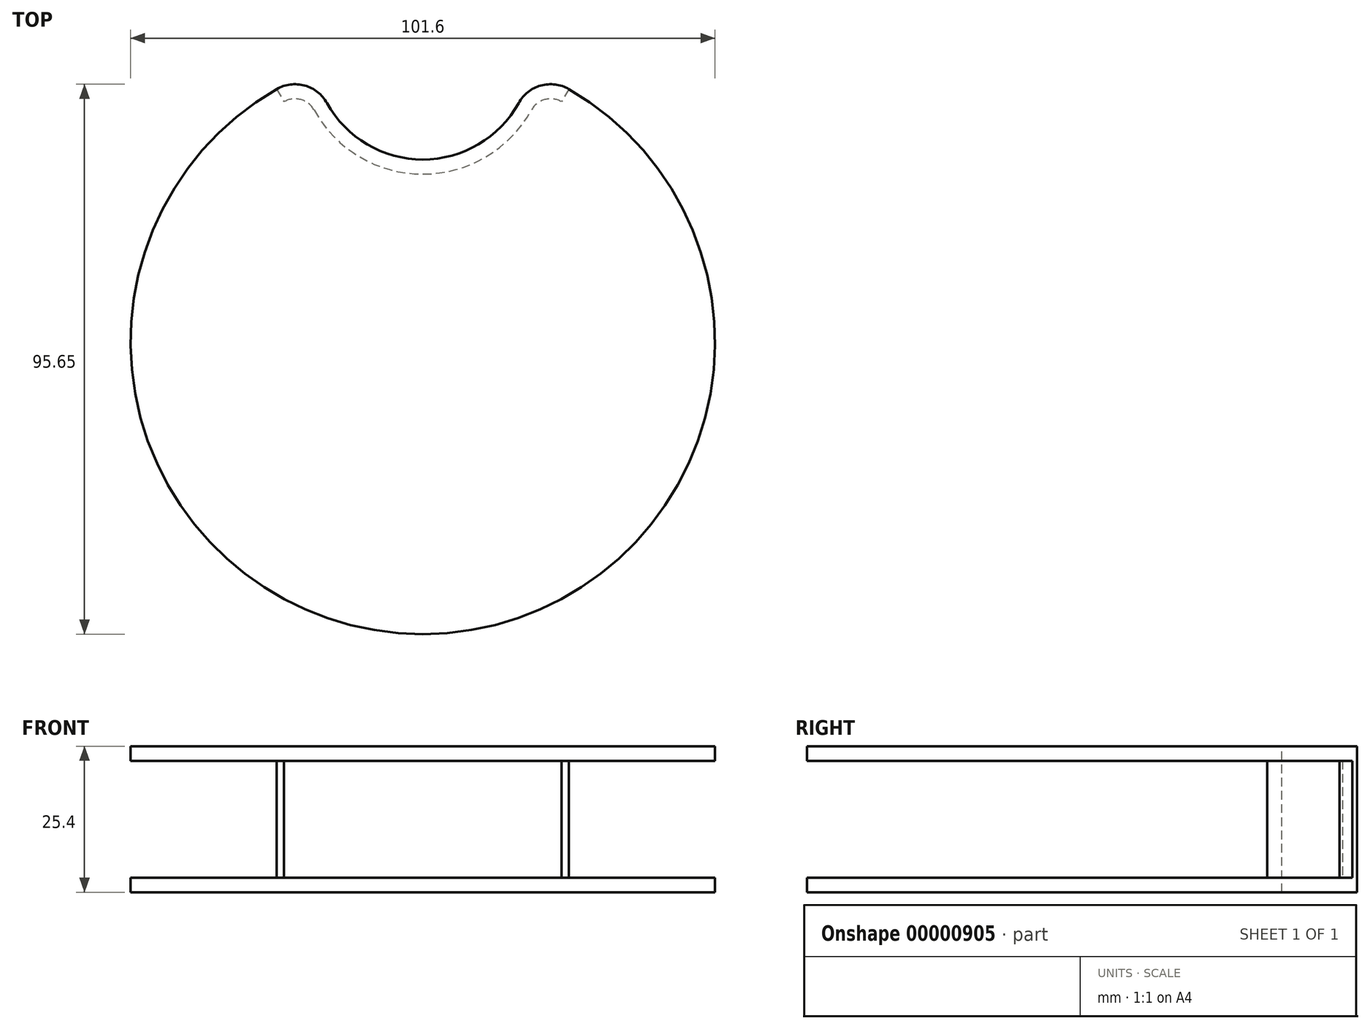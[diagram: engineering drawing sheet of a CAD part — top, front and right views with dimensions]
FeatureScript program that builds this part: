
annotation { "Feature Type Name" : "Feature", "Feature Type Description" : "" }
export const myFeature = defineFeature(function(context is Context, id is Id, definition is map)
    precondition{}
    {
        {
            var Q0;
            Q0=qCreatedBy(makeId("Top.planeOp"),FACE);
            var sketch = newSketch(context, id + "F0", { "sketchPlane" : qUnion([Q0])});
            skCircle(sketch, "E0", {"center": v(0, 0) * mm, "radius": 50.8 * mm});
            skSolve(sketch);
        }
        {
            var Q0;
            Q0 = qSketchRegion(id + "F0", true);
            extrude(context, id + "F1", {"entities" : qUnion([Q0]), "depth" : 25.4 * mm, "symmetric" : true});
        }
        {
            var Q0;
            Q0=makeQuery(id+"F1.opExtrude","CAP_FACE",FACE,{"disambiguationData":[OSD([sQuery(id+"F0.wireOp",EDGE,"E0")])],"isStart":false});
            var sketch = newSketch(context, id + "F2", { "sketchPlane" : qUnion([Q0])});
            skCircle(sketch, "E1", {"center": v(0, 50.8) * mm, "radius": 19.05 * mm});
            skSolve(sketch);
        }
        {
            var Q0;
            Q0 = qSketchRegion(id + "F2", true);
            extrude(context, id + "F3", {"entities" : qUnion([Q0]), "operationType" : NewBodyOperationType.REMOVE, "endBound" : BoundingType.THROUGH_ALL, "oppositeDirection" : true, "depth" : 25.4 * mm});
        }
        {
            var Q0;
            Q0=makeQuery(id+"F3.boolean.opBoolean","INTERSECT",EDGE,{"disambiguationData":[OD(0.0)],"derivedFrom":[makeQuery(id+"F1.opExtrude","SWEPT_FACE",FACE,{"disambiguationData":[OSD([sQuery(id+"F0.wireOp",EDGE,"E0")])]}),makeQuery(id+"F3.opExtrude","SWEPT_FACE",FACE,{"disambiguationData":[OSD([sQuery(id+"F2.wireOp",EDGE,"E1")])]})]});
            var Q1;
            Q1=makeQuery(id+"F3.boolean.opBoolean","INTERSECT",EDGE,{"disambiguationData":[OD(1.0)],"derivedFrom":[makeQuery(id+"F1.opExtrude","SWEPT_FACE",FACE,{"disambiguationData":[OSD([sQuery(id+"F0.wireOp",EDGE,"E0")])]}),makeQuery(id+"F3.opExtrude","SWEPT_FACE",FACE,{"disambiguationData":[OSD([sQuery(id+"F2.wireOp",EDGE,"E1")])]})]});
            var Q2;
            Q2=makeQuery(id+"FYpLOodkCXIoDKC_1.2.F3.boolean.opBoolean","INTERSECT",EDGE,{"disambiguationData":[OD(0.0)],"derivedFrom":[makeQuery(id+"FYpLOodkCXIoDKC_1.1.F3.boolean.opBoolean","SPLIT",FACE,{"disambiguationData":[OD(0.0)],"derivedFrom":makeQuery(id+"F1.opExtrude","SWEPT_FACE",FACE,{"disambiguationData":[OSD([sQuery(id+"F0.wireOp",EDGE,"E0")])]})}),makeQuery(id+"FYpLOodkCXIoDKC_1.2.F3.opExtrude","SWEPT_FACE",FACE,{"disambiguationData":[OSD([sQuery(id+"F2.wireOp",EDGE,"E1")])]})]});
            var Q3;
            Q3=makeQuery(id+"FYpLOodkCXIoDKC_1.2.F3.boolean.opBoolean","INTERSECT",EDGE,{"disambiguationData":[OD(1.0)],"derivedFrom":[makeQuery(id+"FYpLOodkCXIoDKC_1.1.F3.boolean.opBoolean","SPLIT",FACE,{"disambiguationData":[OD(0.0)],"derivedFrom":makeQuery(id+"F1.opExtrude","SWEPT_FACE",FACE,{"disambiguationData":[OSD([sQuery(id+"F0.wireOp",EDGE,"E0")])]})}),makeQuery(id+"FYpLOodkCXIoDKC_1.2.F3.opExtrude","SWEPT_FACE",FACE,{"disambiguationData":[OSD([sQuery(id+"F2.wireOp",EDGE,"E1")])]})]});
            var Q4;
            Q4=makeQuery(id+"FYpLOodkCXIoDKC_1.1.F3.boolean.opBoolean","INTERSECT",EDGE,{"disambiguationData":[OD(0.0)],"derivedFrom":[makeQuery(id+"F1.opExtrude","SWEPT_FACE",FACE,{"disambiguationData":[OSD([sQuery(id+"F0.wireOp",EDGE,"E0")])]}),makeQuery(id+"FYpLOodkCXIoDKC_1.1.F3.opExtrude","SWEPT_FACE",FACE,{"disambiguationData":[OSD([sQuery(id+"F2.wireOp",EDGE,"E1")])]})]});
            var Q5;
            Q5=makeQuery(id+"FYpLOodkCXIoDKC_1.1.F3.boolean.opBoolean","INTERSECT",EDGE,{"disambiguationData":[OD(1.0)],"derivedFrom":[makeQuery(id+"F1.opExtrude","SWEPT_FACE",FACE,{"disambiguationData":[OSD([sQuery(id+"F0.wireOp",EDGE,"E0")])]}),makeQuery(id+"FYpLOodkCXIoDKC_1.1.F3.opExtrude","SWEPT_FACE",FACE,{"disambiguationData":[OSD([sQuery(id+"F2.wireOp",EDGE,"E1")])]})]});
            fillet(context, id + "F4", {"entities" : qUnion([Q0, Q1, Q2, Q3, Q4, Q5]), "radius" : 6.35 * mm, "tangentPropagation" : true, "allowEdgeOverflow" : false});
        }
        {
            var Q0;
            {var subQ0=sQuery(id+"F0.wireOp",EDGE,"E0");var subQ1=sQuery(id+"F2.wireOp",EDGE,"E1");Q0=makeQuery(id+"FYpLOodkCXIoDKC_1.2.F3.boolean.opBoolean","SPLIT",FACE,{"disambiguationData":[TD([makeQuery(id+"FYpLOodkCXIoDKC_1.1.F3.boolean.opBoolean","COPY",FACE,{"derivedFrom":makeQuery(id+"FYpLOodkCXIoDKC_1.1.F3.opExtrude","SWEPT_FACE",FACE,{"disambiguationData":[OSD([subQ1])]})})])],"derivedFrom":makeQuery(id+"FYpLOodkCXIoDKC_1.1.F3.boolean.opBoolean","SPLIT",FACE,{"disambiguationData":[OD(0.0)],"derivedFrom":makeQuery(id+"F1.opExtrude","SWEPT_FACE",FACE,{"disambiguationData":[OSD([subQ0])]})})});}
            var Q1;
            {var subQ0=sQuery(id+"F2.wireOp",EDGE,"E1");var subQ1=sQuery(id+"F0.wireOp",EDGE,"E0");Q1=makeQuery(id+"F4.opFillet","BLEND_FACE",FACE,{"disambiguationData":[OSD([subQ1,subQ0]),TDD([makeQuery(id+"FYpLOodkCXIoDKC_1.1.F3.boolean.opBoolean","INTERSECT",EDGE,{"disambiguationData":[OD(0.0)],"derivedFrom":[makeQuery(id+"F1.opExtrude","SWEPT_FACE",FACE,{"disambiguationData":[OSD([subQ1])]}),makeQuery(id+"FYpLOodkCXIoDKC_1.1.F3.opExtrude","SWEPT_FACE",FACE,{"disambiguationData":[OSD([subQ0])]})]})])]});}
            var Q2;
            {var subQ0=sQuery(id+"F2.wireOp",EDGE,"E1");var subQ1=sQuery(id+"F0.wireOp",EDGE,"E0");Q2=makeQuery(id+"F4.opFillet","BLEND_FACE",FACE,{"disambiguationData":[OSD([subQ1,subQ0]),TDD([makeQuery(id+"FYpLOodkCXIoDKC_1.2.F3.boolean.opBoolean","INTERSECT",EDGE,{"disambiguationData":[OD(1.0)],"derivedFrom":[makeQuery(id+"FYpLOodkCXIoDKC_1.1.F3.boolean.opBoolean","SPLIT",FACE,{"disambiguationData":[OD(0.0)],"derivedFrom":makeQuery(id+"F1.opExtrude","SWEPT_FACE",FACE,{"disambiguationData":[OSD([subQ1])]})}),makeQuery(id+"FYpLOodkCXIoDKC_1.2.F3.opExtrude","SWEPT_FACE",FACE,{"disambiguationData":[OSD([subQ0])]})]})])]});}
            shell(context, id + "F5", {"entities" : qUnion([Q0, Q1, Q2]), "thickness" : 2.54 * mm});
        }
    });
